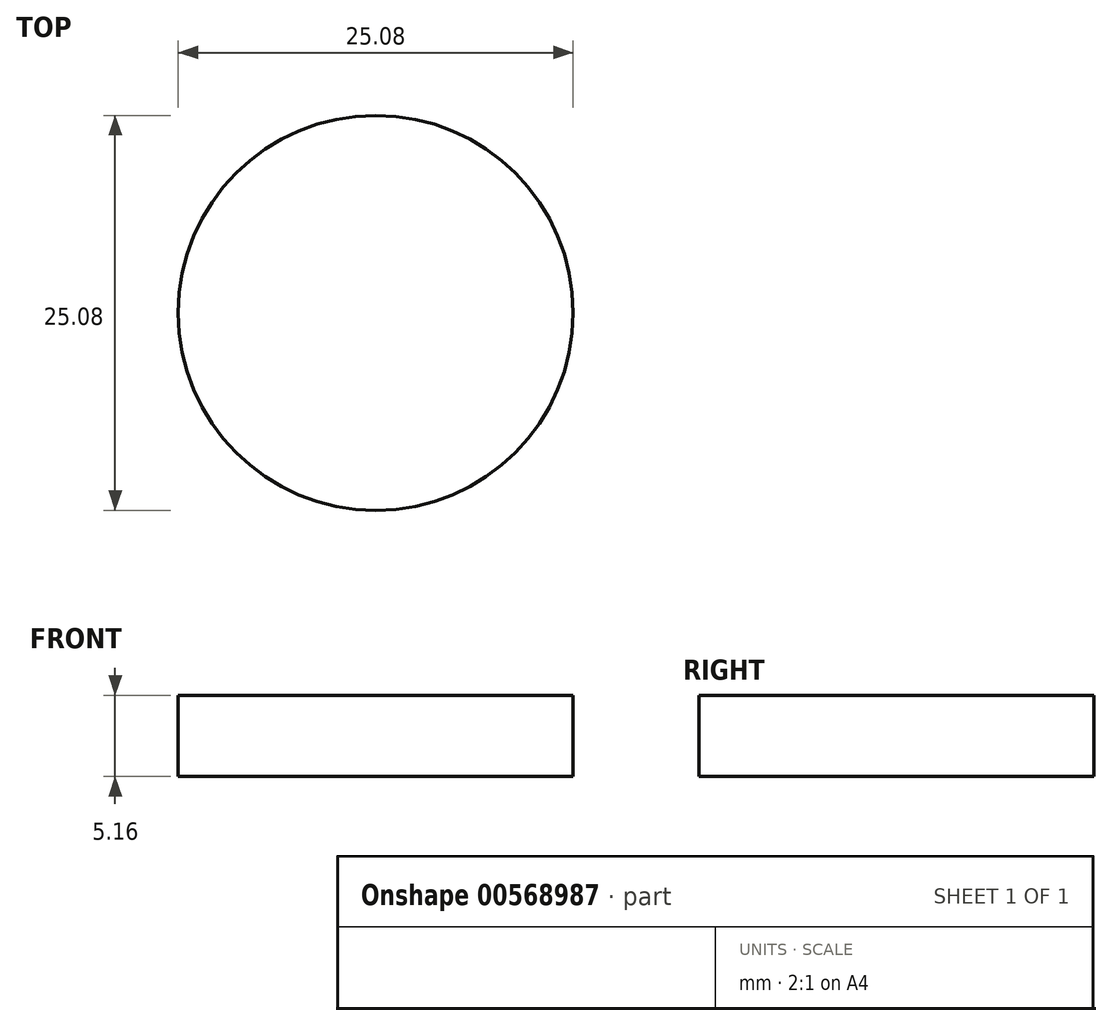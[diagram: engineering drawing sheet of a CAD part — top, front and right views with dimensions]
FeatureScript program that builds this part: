
annotation { "Feature Type Name" : "Feature", "Feature Type Description" : "" }
export const myFeature = defineFeature(function(context is Context, id is Id, definition is map)
    precondition{}
    {
        {
            var Q0;
            Q0=qCreatedBy(makeId("Front.planeOp"),FACE);
            var sketch = newSketch(context, id + "F0", { "sketchPlane" : qUnion([Q0])});
            skLineSegment(sketch, "E0.bottom", {"start": v(-12.54, -3.97) * mm, "end": v(12.54, -3.97) * mm});
            skLineSegment(sketch, "E0.top", {"start": v(-12.54, -9.13) * mm, "end": v(12.54, -9.13) * mm});
            skLineSegment(sketch, "E0.left", {"start": v(-12.54, -3.97) * mm, "end": v(-12.54, -9.13) * mm});
            skLineSegment(sketch, "E0.right", {"start": v(12.54, -3.97) * mm, "end": v(12.54, -9.13) * mm});
            skLineSegment(sketch, "E1", {"start": v(0, -3.97) * mm, "end": v(0, -9.13) * mm});
            skSolve(sketch);
        }
        {
            var Q0;
            {var subQ0=sQuery(id+"F0.wireOp",EDGE,"E0.right");Q0=makeQuery(id+"F0.imprint","IMPRINT",FACE,{"disambiguationData":[TD([[makeQuery(id+"F0.imprint","IMPRINT",EDGE,{"derivedFrom":subQ0}),-1.0]])]});}
            var Q1;
            Q1=sQuery(id+"F0.wireOp",EDGE,"E1");
            revolve(context, id + "F1", {"entities" : qUnion([Q0]), "axis" : qUnion([Q1]), "revolveType" : RevolveType.FULL});
        }
    });
